# Revit family: equip-sink-clsrm-elkay-dbl-lustrtne-l
name_source: partatom
category: Plumbing Fixtures
units: mm (PartAtom-declared; Revit-internal decimal feet)

## family parameters
Always vertical = Yes
Cut with Voids When Loaded = No
OmniClass Number = 23.45.05.14.14.27
OmniClass Title = Service Sinks
Part Type = Normal
Room Calculation Point = No
Round Connector Dimension = Use Radius
Shared = No
Work Plane-Based = Yes

## types (2) — shared parameters
Assembly Code = D2010410
Equal Sized Bowl Formula = 1' - 0 5/8"
Left Bowl Depth = 0' - 3 5/8"
Left Bowl Drain Location = 0' - 6"
Left Bowl Ledge Back Width = 0' - 3 1/2"
Left Bowl Length = 0' - 9 1/4"
Left Bowl Width = 1' - 0"
Left Edge to CL Partition = 1' - 4 3/4"
Left Faucet   Right Bubbler = No
Left Faucet Hole Top = 0' - 0 1/8"
Manufacturer = Elkay Manufacturing
MasterFormat Number = 22.42.16.16
MasterFormat Title = Commercial Sinks
OmniClass Code = 23.45.05.14.14.27
OmniClass Title = Service Sinks
Partition Width = 0' - 6"
Right Bowl Ledge Back Width = 0' - 4"
Right Bowl Length = 1' - 4"
Right Bowl Width = 0' - 11 1/2"
Right Faucet   Left Bubbler = Yes
Right Faucet Hole Top = 0' - 0 1/2"
Sanitary Flow Rate = 10 GPM
Sanitary Nominal Dia = 0' - 1 1/2"
Sanitary Nominal Radius = 0' - 0 3/4"
Sink Ledge Back Width Left Hidden = 0' - 3 1/2"
Sink Ledge Back Width Right Hidden = 0' - 4"
Sink Ledge Front Width = 0' - 1 1/2"
Sink Ledge Front Width Hidden = 0' - 1 1/2"
Sink Ledge Left Width = 0' - 4 1/2"
Sink Ledge Left Width Hidden = 0' - 4 1/2"
Sink Ledge Right Width = 0' - 1 1/2"
Sink Ledge Right Width Hidden = 0' - 1 1/2"
Sink Ledge Sides Width = 0' - 4"
Sink Length = 3' - 1 1/4"
Sink Material = Metal - Steel - Stainless - Chrome
Sink Width = 1' - 5"
Specification Sheet URL = http://www.elkayusa.com
URL = www.elkayusa.com

## per-type parameters (varying)
| type | Default Elevation | Description | Model | Right Bowl Depth | Right Bowl Drain Location |
| DRKR3717L | 4' - 0" | Lustertone Double Bowl Sink | DRKR3717L | 0' - 7 5/8" | 0' - 5 3/4" |
| DRKAD371740L | 3' - 0" | Lustertone Classroom Double Bowl Sink | DRKAD3717L | 0' - 4" | 0' - 5" |

## geometry (parser evidence)
native form markers: Sweep x5
no freeform markers — native parametric forms only
